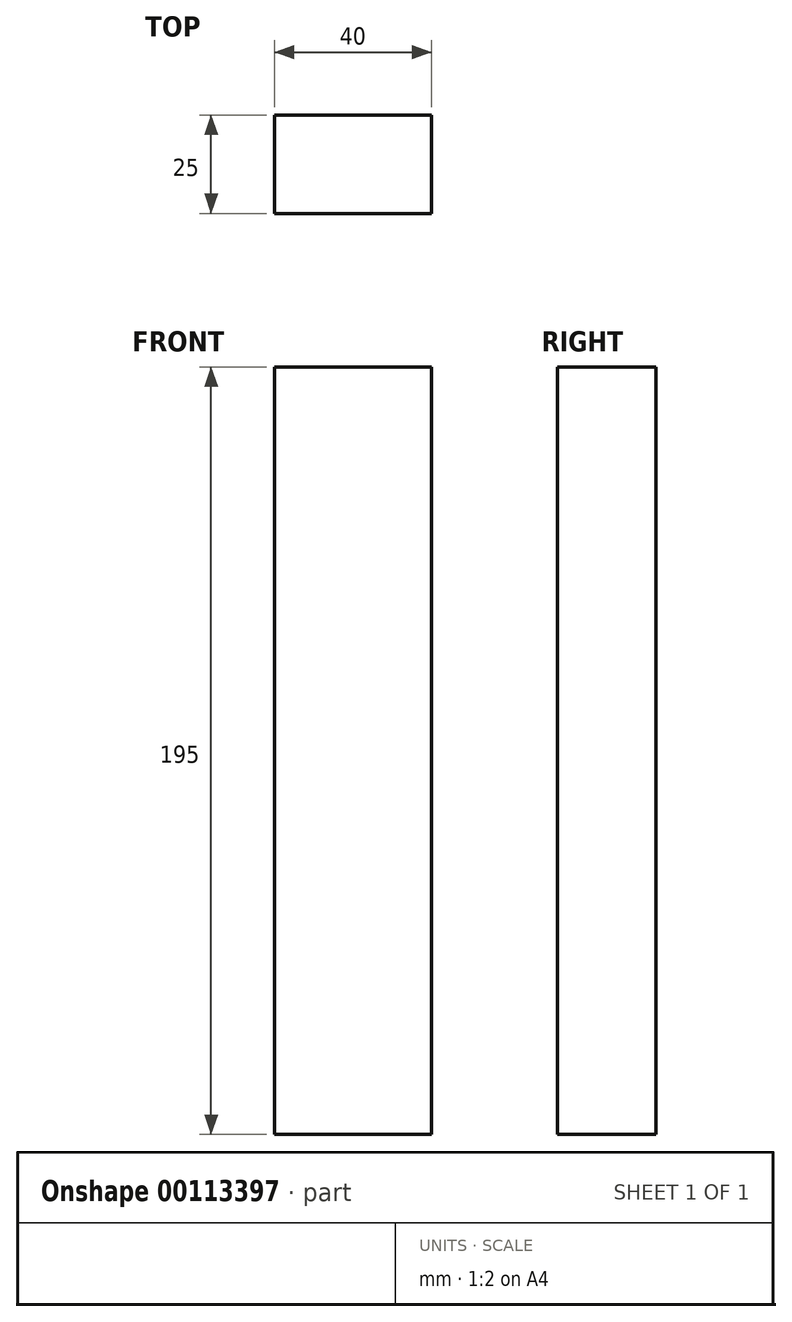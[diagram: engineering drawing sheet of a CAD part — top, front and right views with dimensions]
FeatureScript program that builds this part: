
annotation { "Feature Type Name" : "Feature", "Feature Type Description" : "" }
export const myFeature = defineFeature(function(context is Context, id is Id, definition is map)
    precondition{}
    {
        {
            var Q0;
            Q0=qCreatedBy(makeId("Front.planeOp"),FACE);
            var sketch = newSketch(context, id + "F0", { "sketchPlane" : qUnion([Q0])});
            skLineSegment(sketch, "E0", {"start": v(0, 0) * mm, "end": v(0, 195) * mm});
            skLineSegment(sketch, "E1", {"start": v(0, 195) * mm, "end": v(40, 195) * mm});
            skLineSegment(sketch, "E2", {"start": v(40, 195) * mm, "end": v(40, 0) * mm});
            skLineSegment(sketch, "E3", {"start": v(40, 0) * mm, "end": v(0, 0) * mm});
            skSolve(sketch);
        }
        {
            var Q0;
            Q0=makeQuery(id+"F0.imprint","IMPRINT",FACE,{"disambiguationData":[TD([[makeQuery(id+"F0.imprint","IMPRINT",EDGE,{"derivedFrom":sQuery(id+"F0.wireOp",EDGE,"E0")}),-1.0]])]});
            extrude(context, id + "F1", {"entities" : qUnion([Q0]), "depth" : 25 * mm});
        }
    });
